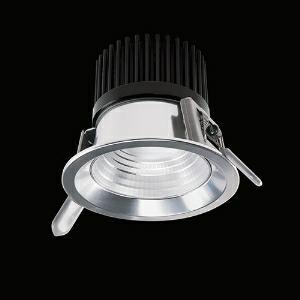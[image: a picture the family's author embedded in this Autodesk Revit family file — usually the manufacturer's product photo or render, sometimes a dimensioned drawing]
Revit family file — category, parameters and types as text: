
# Revit family: spectral_myral_myral_4500-830-s
name_source: partatom
category: Lighting Fixtures
revit_build: Autodesk Revit 2016 (Build: 20150220_1215(x64)
units: mm (PartAtom-declared; Revit-internal decimal feet)

## family parameters
Cut with Voids When Loaded = No
Host = Face
Light Source = No
Part Type = Normal
Room Calculation Point = No
Round Connector Dimension = Use Diameter
Shared = No

## types (1)
- SPECTRAL MYRAL (1 x )
    Apparent Load = 0 VA
    Approval mark = CE
    CIE Flux Codes = 85 100 100 100 100
    Control Gear = Electronic transformer
    Default Elevation = 1800 mm
    Description = SPG0320176
MYRAL recessed spot

Design:
    Height = 0 mm  [stored 0 ft]
    Lamp = 1 x
    Lamp count = 1
    Length = 120 mm
    Luminous efficacy = 0 lm/W
    Manufacturer = Ridi
    ModVariant = No
    Model = MYRAL 4500-830-S
    Mounting Place = Ceiling
    Mounting Type = Recessed
    Number of Poles = 1
    OnlyDefault = Yes
    Power Factor = 1
    Product Name = SPECTRAL MYRAL
    Product group = Downlight recessed
    ProductGroupID = 400
    Protection Class = Protection class
    Protection Degree = IP 20
    RlxData = <blob elided: 38881 chars, md5=59dc47c7>
    Socket = socket
    Standby Power = 0 W
    System Light Flux = 0 lm
    System Power = 0 W
    Type Image = myral_04.jpg
    URL = http://reluxnet.relux.com
    VarID = ---
    Voltage = 0 V
    Weight = 0.00 kg
    Width = 0 mm  [stored 0 ft]

note: [stored X ft] marks values corroborated as IEEE doubles in the binary element streams (Revit-internal decimal feet)

## geometry (parser evidence)
native form markers: Sweep x11
no freeform markers — native parametric forms only
